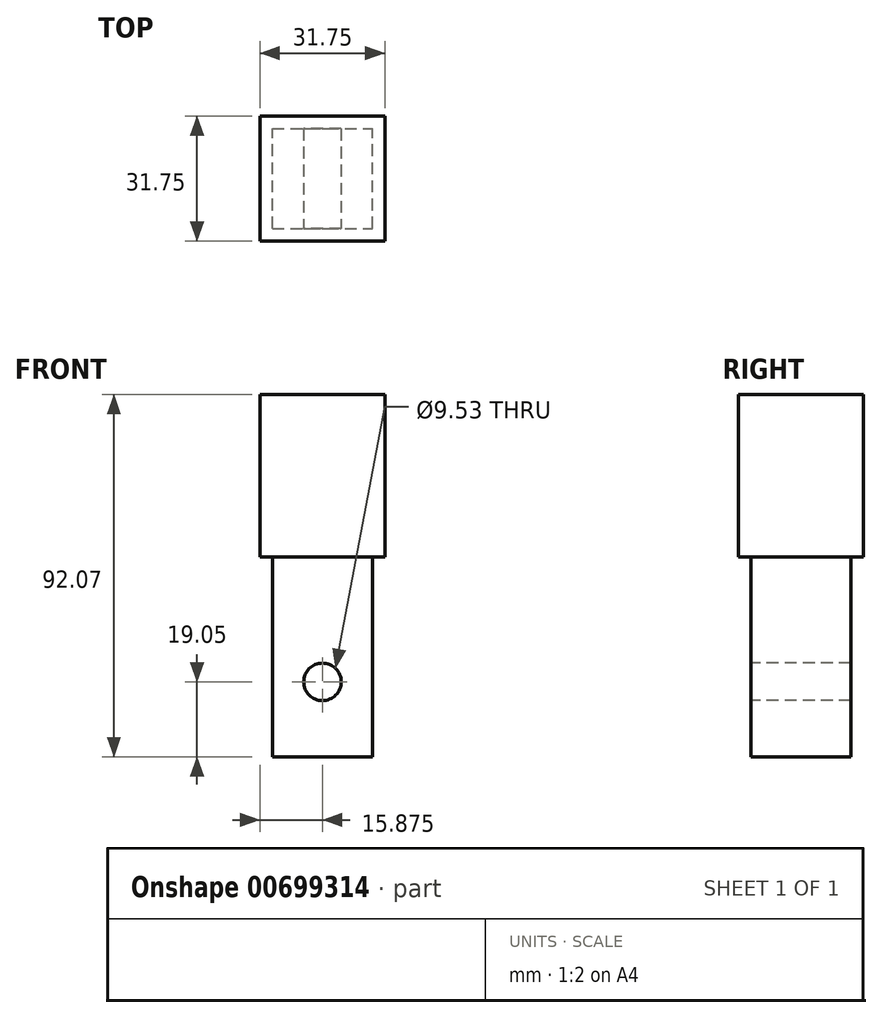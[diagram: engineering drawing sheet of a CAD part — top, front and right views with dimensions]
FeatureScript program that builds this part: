
annotation { "Feature Type Name" : "Feature", "Feature Type Description" : "" }
export const myFeature = defineFeature(function(context is Context, id is Id, definition is map)
    precondition{}
    {
        {
            var Q0;
            Q0=qCreatedBy(makeId("Top.planeOp"),FACE);
            var sketch = newSketch(context, id + "F0", { "sketchPlane" : qUnion([Q0])});
            skLineSegment(sketch, "E0.bottom", {"start": v(0, 0) * mm, "end": v(31.75, 0) * mm});
            skLineSegment(sketch, "E0.top", {"start": v(0, 31.75) * mm, "end": v(31.75, 31.75) * mm});
            skLineSegment(sketch, "E0.left", {"start": v(0, 0) * mm, "end": v(0, 31.75) * mm});
            skLineSegment(sketch, "E0.right", {"start": v(31.75, 0) * mm, "end": v(31.75, 31.75) * mm});
            skSolve(sketch);
        }
        {
            var Q0;
            Q0=makeQuery(id+"F0.imprint","IMPRINT",FACE,{"disambiguationData":[TD([[makeQuery(id+"F0.imprint","IMPRINT",EDGE,{"derivedFrom":sQuery(id+"F0.wireOp",EDGE,"E0.bottom")}),1.0]])]});
            extrude(context, id + "F1", {"entities" : qUnion([Q0]), "depth" : 41.27 * mm, "offsetDistance" : 25.4 * mm});
        }
        {
            var Q0;
            Q0=makeQuery(id+"F1.opExtrude","CAP_FACE",FACE,{"disambiguationData":[OSD([sQuery(id+"F0.wireOp",EDGE,"E0.bottom"),sQuery(id+"F0.wireOp",EDGE,"E0.top"),sQuery(id+"F0.wireOp",EDGE,"E0.left"),sQuery(id+"F0.wireOp",EDGE,"E0.right")])],"isStart":true});
            var sketch = newSketch(context, id + "F2", { "sketchPlane" : qUnion([Q0])});
            skLineSegment(sketch, "E1.0", {"start": v(3.18, -3.18) * mm, "end": v(3.18, -28.57) * mm});
            skLineSegment(sketch, "E1.1", {"start": v(3.18, -3.18) * mm, "end": v(28.58, -3.18) * mm});
            skLineSegment(sketch, "E1.2", {"start": v(28.58, -3.18) * mm, "end": v(28.57, -28.57) * mm});
            skLineSegment(sketch, "E1.3", {"start": v(3.18, -28.57) * mm, "end": v(28.57, -28.57) * mm});
            skLineSegment(sketch, "E2.0", {"start": v(-6.35, -38.1) * mm, "end": v(38.1, -38.1) * mm});
            skLineSegment(sketch, "E2.1", {"start": v(-6.35, 6.35) * mm, "end": v(-6.35, -38.1) * mm});
            skLineSegment(sketch, "E2.2", {"start": v(38.1, 6.35) * mm, "end": v(-6.35, 6.35) * mm});
            skLineSegment(sketch, "E2.3", {"start": v(38.1, -38.1) * mm, "end": v(38.1, 6.35) * mm});
            skSolve(sketch);
        }
        {
            var Q0;
            Q0=makeQuery(id+"F2.imprint","IMPRINT",FACE,{"disambiguationData":[TD([[makeQuery(id+"F2.imprint","IMPRINT",EDGE,{"derivedFrom":sQuery(id+"F2.wireOp",EDGE,"E1.0")}),1.0]])]});
            extrude(context, id + "F3", {"entities" : qUnion([Q0]), "operationType" : NewBodyOperationType.ADD, "depth" : 50.8 * mm, "offsetDistance" : 25.4 * mm});
        }
        {
            var Q0;
            Q0=makeQuery(id+"F3.opExtrude","SWEPT_FACE",FACE,{"disambiguationData":[OSD([sQuery(id+"F2.wireOp",EDGE,"E1.1")])]});
            var sketch = newSketch(context, id + "F4", { "sketchPlane" : qUnion([Q0])});
            skCircle(sketch, "E3", {"center": v(15.87, -31.75) * mm, "radius": 4.76 * mm});
            skPoint(sketch, "E3.centerSnap0", {"position": v(28.58, -25.4) * mm});
            skPoint(sketch, "E3.centerSnap1", {"position": v(15.88, -50.8) * mm});
            skSolve(sketch);
        }
        {
            var Q0;
            Q0=makeQuery(id+"F4.imprint","IMPRINT",FACE,{"disambiguationData":[TD([[makeQuery(id+"F4.imprint","IMPRINT",EDGE,{"derivedFrom":sQuery(id+"F4.wireOp",EDGE,"E3")}),1.0]])]});
            extrude(context, id + "F5", {"entities" : qUnion([Q0]), "operationType" : NewBodyOperationType.REMOVE, "endBound" : BoundingType.THROUGH_ALL, "oppositeDirection" : true, "depth" : 25.4 * mm, "offsetDistance" : 25.4 * mm});
        }
    });
